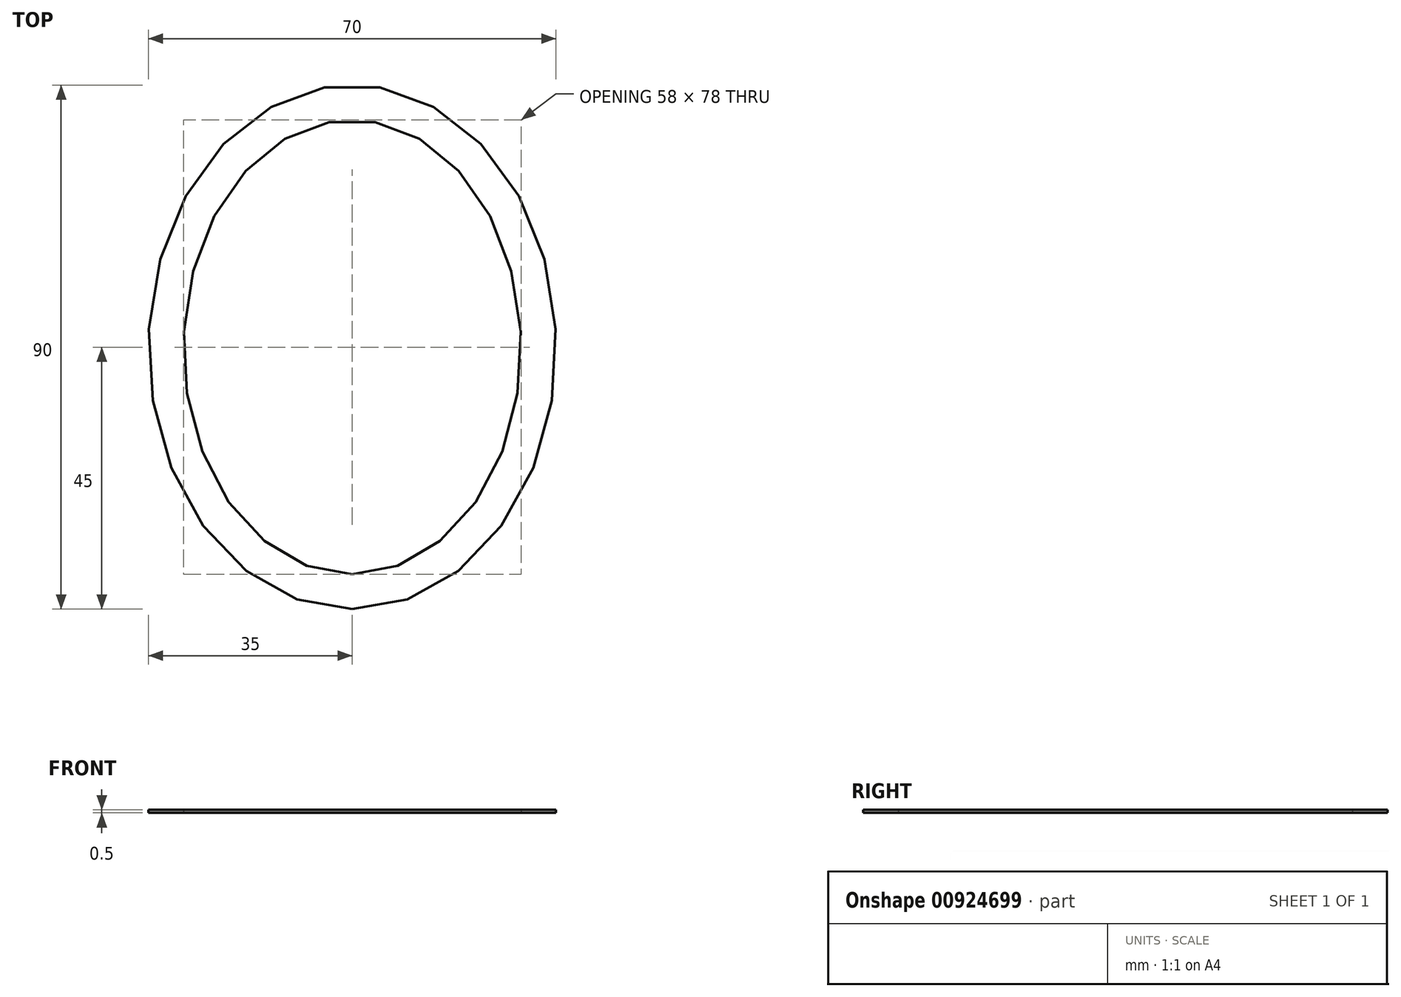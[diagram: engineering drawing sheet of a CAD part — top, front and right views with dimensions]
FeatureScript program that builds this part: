
annotation { "Feature Type Name" : "Feature", "Feature Type Description" : "" }
export const myFeature = defineFeature(function(context is Context, id is Id, definition is map)
    precondition{}
    {
        {
            var Q0;
            Q0=qCreatedBy(makeId("Top.planeOp"),FACE);
            var sketch = newSketch(context, id + "F0", { "sketchPlane" : qUnion([Q0])});
            skEllipse(sketch, "E0", {"center": v(0, 0) * mm, "majorRadius": 39 * mm, "minorRadius": 29 * mm, "majorAxis": v(0, -1)});
            skEllipse(sketch, "E1", {"center": v(0, 0) * mm, "majorRadius": 45 * mm, "minorRadius": 35 * mm, "majorAxis": v(0, -1)});
            skSolve(sketch);
        }
        {
            var Q0;
            Q0=makeQuery(id+"F0.imprint","IMPRINT",FACE,{"disambiguationData":[TD([[makeQuery(id+"F0.imprint","IMPRINT",EDGE,{"derivedFrom":sQuery(id+"F0.wireOp",EDGE,"E0")}),-1.0]])]});
            extrude(context, id + "F1", {"entities" : qUnion([Q0]), "depth" : 0.5 * mm, "offsetDistance" : 25 * mm});
        }
    });
